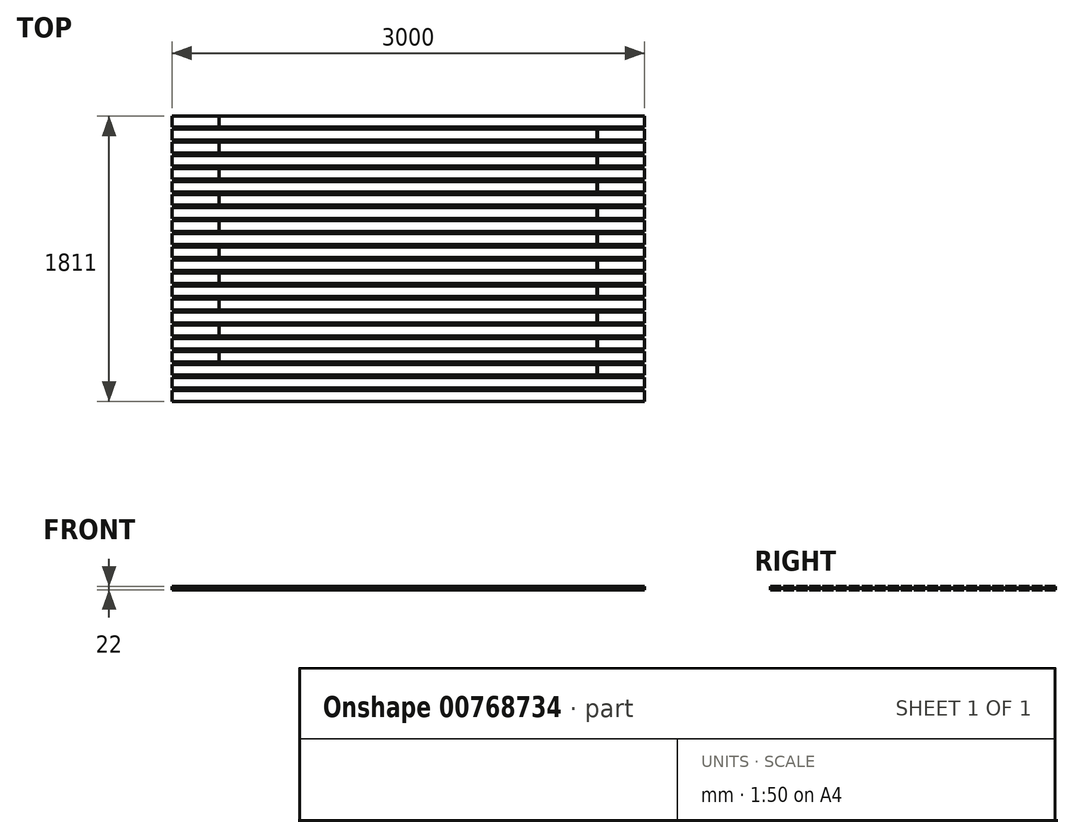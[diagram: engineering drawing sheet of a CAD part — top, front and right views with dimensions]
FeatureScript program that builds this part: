
annotation { "Feature Type Name" : "Feature", "Feature Type Description" : "" }
export const myFeature = defineFeature(function(context is Context, id is Id, definition is map)
    precondition{}
    {
        {
            var Q0;
            Q0=qCreatedBy(makeId("Top.planeOp"),FACE);
            var sketch = newSketch(context, id + "F0", { "sketchPlane" : qUnion([Q0])});
            skLineSegment(sketch, "E0.bottom", {"start": v(0, 0) * mm, "end": v(2700, 0) * mm});
            skLineSegment(sketch, "E0.top", {"start": v(0, 68) * mm, "end": v(2700, 68) * mm});
            skLineSegment(sketch, "E0.left", {"start": v(0, 0) * mm, "end": v(0, 68) * mm});
            skLineSegment(sketch, "E0.right", {"start": v(2700, 0) * mm, "end": v(2700, 68) * mm});
            skLineSegment(sketch, "E1.bottom", {"start": v(0, 83) * mm, "end": v(300, 83) * mm});
            skLineSegment(sketch, "E1.top", {"start": v(0, 151) * mm, "end": v(300, 151) * mm});
            skLineSegment(sketch, "E1.left", {"start": v(0, 83) * mm, "end": v(0, 151) * mm});
            skLineSegment(sketch, "E1.right", {"start": v(300, 83) * mm, "end": v(300, 151) * mm});
            skLineSegment(sketch, "E2.bottom", {"start": v(300, 151) * mm, "end": v(3000, 151) * mm});
            skLineSegment(sketch, "E2.top", {"start": v(300, 83) * mm, "end": v(3000, 83) * mm});
            skLineSegment(sketch, "E2.left", {"start": v(300, 151) * mm, "end": v(300, 83) * mm});
            skLineSegment(sketch, "E2.right", {"start": v(3000, 151) * mm, "end": v(3000, 83) * mm});
            skLineSegment(sketch, "E3.bottom", {"start": v(2700, 68) * mm, "end": v(3000, 68) * mm});
            skLineSegment(sketch, "E3.top", {"start": v(2700, 0) * mm, "end": v(3000, 0) * mm});
            skLineSegment(sketch, "E3.left", {"start": v(2700, 68) * mm, "end": v(2700, 0) * mm});
            skLineSegment(sketch, "E3.right", {"start": v(3000, 68) * mm, "end": v(3000, 0) * mm});
            skLineSegment(sketch, "E4.0.1.0", {"start": v(0, 249) * mm, "end": v(300, 249) * mm});
            skLineSegment(sketch, "E4.0.1.1", {"start": v(0, 234) * mm, "end": v(2700, 234) * mm});
            skLineSegment(sketch, "E4.0.1.2", {"start": v(300, 317) * mm, "end": v(3000, 317) * mm});
            skLineSegment(sketch, "E4.0.1.3", {"start": v(0, 317) * mm, "end": v(300, 317) * mm});
            skLineSegment(sketch, "E4.0.1.4", {"start": v(2700, 166) * mm, "end": v(3000, 166) * mm});
            skLineSegment(sketch, "E4.0.1.5", {"start": v(2700, 234) * mm, "end": v(3000, 234) * mm});
            skLineSegment(sketch, "E4.0.1.6", {"start": v(300, 249) * mm, "end": v(3000, 249) * mm});
            skLineSegment(sketch, "E4.0.1.7", {"start": v(0, 166) * mm, "end": v(2700, 166) * mm});
            skLineSegment(sketch, "E4.0.1.8", {"start": v(3000, 234) * mm, "end": v(3000, 166) * mm});
            skLineSegment(sketch, "E4.0.1.9", {"start": v(0, 166) * mm, "end": v(0, 234) * mm});
            skLineSegment(sketch, "E4.0.1.10", {"start": v(0, 249) * mm, "end": v(0, 317) * mm});
            skLineSegment(sketch, "E4.0.1.11", {"start": v(3000, 317) * mm, "end": v(3000, 249) * mm});
            skLineSegment(sketch, "E4.0.1.12", {"start": v(2700, 234) * mm, "end": v(2700, 166) * mm});
            skLineSegment(sketch, "E4.0.1.13", {"start": v(300, 317) * mm, "end": v(300, 249) * mm});
            skLineSegment(sketch, "E4.0.1.14", {"start": v(300, 249) * mm, "end": v(300, 317) * mm});
            skLineSegment(sketch, "E4.0.1.15", {"start": v(2700, 166) * mm, "end": v(2700, 234) * mm});
            skLineSegment(sketch, "E4.0.2.0", {"start": v(0, 415) * mm, "end": v(300, 415) * mm});
            skLineSegment(sketch, "E4.0.2.1", {"start": v(0, 400) * mm, "end": v(2700, 400) * mm});
            skLineSegment(sketch, "E4.0.2.2", {"start": v(300, 483) * mm, "end": v(3000, 483) * mm});
            skLineSegment(sketch, "E4.0.2.3", {"start": v(0, 483) * mm, "end": v(300, 483) * mm});
            skLineSegment(sketch, "E4.0.2.4", {"start": v(2700, 332) * mm, "end": v(3000, 332) * mm});
            skLineSegment(sketch, "E4.0.2.5", {"start": v(2700, 400) * mm, "end": v(3000, 400) * mm});
            skLineSegment(sketch, "E4.0.2.6", {"start": v(300, 415) * mm, "end": v(3000, 415) * mm});
            skLineSegment(sketch, "E4.0.2.7", {"start": v(0, 332) * mm, "end": v(2700, 332) * mm});
            skLineSegment(sketch, "E4.0.2.8", {"start": v(3000, 400) * mm, "end": v(3000, 332) * mm});
            skLineSegment(sketch, "E4.0.2.9", {"start": v(0, 332) * mm, "end": v(0, 400) * mm});
            skLineSegment(sketch, "E4.0.2.10", {"start": v(0, 415) * mm, "end": v(0, 483) * mm});
            skLineSegment(sketch, "E4.0.2.11", {"start": v(3000, 483) * mm, "end": v(3000, 415) * mm});
            skLineSegment(sketch, "E4.0.2.12", {"start": v(2700, 400) * mm, "end": v(2700, 332) * mm});
            skLineSegment(sketch, "E4.0.2.13", {"start": v(300, 483) * mm, "end": v(300, 415) * mm});
            skLineSegment(sketch, "E4.0.2.14", {"start": v(300, 415) * mm, "end": v(300, 483) * mm});
            skLineSegment(sketch, "E4.0.2.15", {"start": v(2700, 332) * mm, "end": v(2700, 400) * mm});
            skLineSegment(sketch, "E4.0.3.0", {"start": v(0, 581) * mm, "end": v(300, 581) * mm});
            skLineSegment(sketch, "E4.0.3.1", {"start": v(0, 566) * mm, "end": v(2700, 566) * mm});
            skLineSegment(sketch, "E4.0.3.2", {"start": v(300, 649) * mm, "end": v(3000, 649) * mm});
            skLineSegment(sketch, "E4.0.3.3", {"start": v(0, 649) * mm, "end": v(300, 649) * mm});
            skLineSegment(sketch, "E4.0.3.4", {"start": v(2700, 498) * mm, "end": v(3000, 498) * mm});
            skLineSegment(sketch, "E4.0.3.5", {"start": v(2700, 566) * mm, "end": v(3000, 566) * mm});
            skLineSegment(sketch, "E4.0.3.6", {"start": v(300, 581) * mm, "end": v(3000, 581) * mm});
            skLineSegment(sketch, "E4.0.3.7", {"start": v(0, 498) * mm, "end": v(2700, 498) * mm});
            skLineSegment(sketch, "E4.0.3.8", {"start": v(3000, 566) * mm, "end": v(3000, 498) * mm});
            skLineSegment(sketch, "E4.0.3.9", {"start": v(0, 498) * mm, "end": v(0, 566) * mm});
            skLineSegment(sketch, "E4.0.3.10", {"start": v(0, 581) * mm, "end": v(0, 649) * mm});
            skLineSegment(sketch, "E4.0.3.11", {"start": v(3000, 649) * mm, "end": v(3000, 581) * mm});
            skLineSegment(sketch, "E4.0.3.12", {"start": v(2700, 566) * mm, "end": v(2700, 498) * mm});
            skLineSegment(sketch, "E4.0.3.13", {"start": v(300, 649) * mm, "end": v(300, 581) * mm});
            skLineSegment(sketch, "E4.0.3.14", {"start": v(300, 581) * mm, "end": v(300, 649) * mm});
            skLineSegment(sketch, "E4.0.3.15", {"start": v(2700, 498) * mm, "end": v(2700, 566) * mm});
            skLineSegment(sketch, "E4.0.4.0", {"start": v(0, 747) * mm, "end": v(300, 747) * mm});
            skLineSegment(sketch, "E4.0.4.1", {"start": v(0, 732) * mm, "end": v(2700, 732) * mm});
            skLineSegment(sketch, "E4.0.4.2", {"start": v(300, 815) * mm, "end": v(3000, 815) * mm});
            skLineSegment(sketch, "E4.0.4.3", {"start": v(0, 815) * mm, "end": v(300, 815) * mm});
            skLineSegment(sketch, "E4.0.4.4", {"start": v(2700, 664) * mm, "end": v(3000, 664) * mm});
            skLineSegment(sketch, "E4.0.4.5", {"start": v(2700, 732) * mm, "end": v(3000, 732) * mm});
            skLineSegment(sketch, "E4.0.4.6", {"start": v(300, 747) * mm, "end": v(3000, 747) * mm});
            skLineSegment(sketch, "E4.0.4.7", {"start": v(0, 664) * mm, "end": v(2700, 664) * mm});
            skLineSegment(sketch, "E4.0.4.8", {"start": v(3000, 732) * mm, "end": v(3000, 664) * mm});
            skLineSegment(sketch, "E4.0.4.9", {"start": v(0, 664) * mm, "end": v(0, 732) * mm});
            skLineSegment(sketch, "E4.0.4.10", {"start": v(0, 747) * mm, "end": v(0, 815) * mm});
            skLineSegment(sketch, "E4.0.4.11", {"start": v(3000, 815) * mm, "end": v(3000, 747) * mm});
            skLineSegment(sketch, "E4.0.4.12", {"start": v(2700, 732) * mm, "end": v(2700, 664) * mm});
            skLineSegment(sketch, "E4.0.4.13", {"start": v(300, 815) * mm, "end": v(300, 747) * mm});
            skLineSegment(sketch, "E4.0.4.14", {"start": v(300, 747) * mm, "end": v(300, 815) * mm});
            skLineSegment(sketch, "E4.0.4.15", {"start": v(2700, 664) * mm, "end": v(2700, 732) * mm});
            skLineSegment(sketch, "E4.0.5.0", {"start": v(0, 913) * mm, "end": v(300, 913) * mm});
            skLineSegment(sketch, "E4.0.5.1", {"start": v(0, 898) * mm, "end": v(2700, 898) * mm});
            skLineSegment(sketch, "E4.0.5.2", {"start": v(300, 981) * mm, "end": v(3000, 981) * mm});
            skLineSegment(sketch, "E4.0.5.3", {"start": v(0, 981) * mm, "end": v(300, 981) * mm});
            skLineSegment(sketch, "E4.0.5.4", {"start": v(2700, 830) * mm, "end": v(3000, 830) * mm});
            skLineSegment(sketch, "E4.0.5.5", {"start": v(2700, 898) * mm, "end": v(3000, 898) * mm});
            skLineSegment(sketch, "E4.0.5.6", {"start": v(300, 913) * mm, "end": v(3000, 913) * mm});
            skLineSegment(sketch, "E4.0.5.7", {"start": v(0, 830) * mm, "end": v(2700, 830) * mm});
            skLineSegment(sketch, "E4.0.5.8", {"start": v(3000, 898) * mm, "end": v(3000, 830) * mm});
            skLineSegment(sketch, "E4.0.5.9", {"start": v(0, 830) * mm, "end": v(0, 898) * mm});
            skLineSegment(sketch, "E4.0.5.10", {"start": v(0, 913) * mm, "end": v(0, 981) * mm});
            skLineSegment(sketch, "E4.0.5.11", {"start": v(3000, 981) * mm, "end": v(3000, 913) * mm});
            skLineSegment(sketch, "E4.0.5.12", {"start": v(2700, 898) * mm, "end": v(2700, 830) * mm});
            skLineSegment(sketch, "E4.0.5.13", {"start": v(300, 981) * mm, "end": v(300, 913) * mm});
            skLineSegment(sketch, "E4.0.5.14", {"start": v(300, 913) * mm, "end": v(300, 981) * mm});
            skLineSegment(sketch, "E4.0.5.15", {"start": v(2700, 830) * mm, "end": v(2700, 898) * mm});
            skLineSegment(sketch, "E4.0.6.0", {"start": v(0, 1079) * mm, "end": v(300, 1079) * mm});
            skLineSegment(sketch, "E4.0.6.1", {"start": v(0, 1064) * mm, "end": v(2700, 1064) * mm});
            skLineSegment(sketch, "E4.0.6.2", {"start": v(300, 1147) * mm, "end": v(3000, 1147) * mm});
            skLineSegment(sketch, "E4.0.6.3", {"start": v(0, 1147) * mm, "end": v(300, 1147) * mm});
            skLineSegment(sketch, "E4.0.6.4", {"start": v(2700, 996) * mm, "end": v(3000, 996) * mm});
            skLineSegment(sketch, "E4.0.6.5", {"start": v(2700, 1064) * mm, "end": v(3000, 1064) * mm});
            skLineSegment(sketch, "E4.0.6.6", {"start": v(300, 1079) * mm, "end": v(3000, 1079) * mm});
            skLineSegment(sketch, "E4.0.6.7", {"start": v(0, 996) * mm, "end": v(2700, 996) * mm});
            skLineSegment(sketch, "E4.0.6.8", {"start": v(3000, 1064) * mm, "end": v(3000, 996) * mm});
            skLineSegment(sketch, "E4.0.6.9", {"start": v(0, 996) * mm, "end": v(0, 1064) * mm});
            skLineSegment(sketch, "E4.0.6.10", {"start": v(0, 1079) * mm, "end": v(0, 1147) * mm});
            skLineSegment(sketch, "E4.0.6.11", {"start": v(3000, 1147) * mm, "end": v(3000, 1079) * mm});
            skLineSegment(sketch, "E4.0.6.12", {"start": v(2700, 1064) * mm, "end": v(2700, 996) * mm});
            skLineSegment(sketch, "E4.0.6.13", {"start": v(300, 1147) * mm, "end": v(300, 1079) * mm});
            skLineSegment(sketch, "E4.0.6.14", {"start": v(300, 1079) * mm, "end": v(300, 1147) * mm});
            skLineSegment(sketch, "E4.0.6.15", {"start": v(2700, 996) * mm, "end": v(2700, 1064) * mm});
            skLineSegment(sketch, "E4.0.7.0", {"start": v(0, 1245) * mm, "end": v(300, 1245) * mm});
            skLineSegment(sketch, "E4.0.7.1", {"start": v(0, 1230) * mm, "end": v(2700, 1230) * mm});
            skLineSegment(sketch, "E4.0.7.2", {"start": v(300, 1313) * mm, "end": v(3000, 1313) * mm});
            skLineSegment(sketch, "E4.0.7.3", {"start": v(0, 1313) * mm, "end": v(300, 1313) * mm});
            skLineSegment(sketch, "E4.0.7.4", {"start": v(2700, 1162) * mm, "end": v(3000, 1162) * mm});
            skLineSegment(sketch, "E4.0.7.5", {"start": v(2700, 1230) * mm, "end": v(3000, 1230) * mm});
            skLineSegment(sketch, "E4.0.7.6", {"start": v(300, 1245) * mm, "end": v(3000, 1245) * mm});
            skLineSegment(sketch, "E4.0.7.7", {"start": v(0, 1162) * mm, "end": v(2700, 1162) * mm});
            skLineSegment(sketch, "E4.0.7.8", {"start": v(3000, 1230) * mm, "end": v(3000, 1162) * mm});
            skLineSegment(sketch, "E4.0.7.9", {"start": v(0, 1162) * mm, "end": v(0, 1230) * mm});
            skLineSegment(sketch, "E4.0.7.10", {"start": v(0, 1245) * mm, "end": v(0, 1313) * mm});
            skLineSegment(sketch, "E4.0.7.11", {"start": v(3000, 1313) * mm, "end": v(3000, 1245) * mm});
            skLineSegment(sketch, "E4.0.7.12", {"start": v(2700, 1230) * mm, "end": v(2700, 1162) * mm});
            skLineSegment(sketch, "E4.0.7.13", {"start": v(300, 1313) * mm, "end": v(300, 1245) * mm});
            skLineSegment(sketch, "E4.0.7.14", {"start": v(300, 1245) * mm, "end": v(300, 1313) * mm});
            skLineSegment(sketch, "E4.0.7.15", {"start": v(2700, 1162) * mm, "end": v(2700, 1230) * mm});
            skLineSegment(sketch, "E4.0.8.0", {"start": v(0, 1411) * mm, "end": v(300, 1411) * mm});
            skLineSegment(sketch, "E4.0.8.1", {"start": v(0, 1396) * mm, "end": v(2700, 1396) * mm});
            skLineSegment(sketch, "E4.0.8.2", {"start": v(300, 1479) * mm, "end": v(3000, 1479) * mm});
            skLineSegment(sketch, "E4.0.8.3", {"start": v(0, 1479) * mm, "end": v(300, 1479) * mm});
            skLineSegment(sketch, "E4.0.8.4", {"start": v(2700, 1328) * mm, "end": v(3000, 1328) * mm});
            skLineSegment(sketch, "E4.0.8.5", {"start": v(2700, 1396) * mm, "end": v(3000, 1396) * mm});
            skLineSegment(sketch, "E4.0.8.6", {"start": v(300, 1411) * mm, "end": v(3000, 1411) * mm});
            skLineSegment(sketch, "E4.0.8.7", {"start": v(0, 1328) * mm, "end": v(2700, 1328) * mm});
            skLineSegment(sketch, "E4.0.8.8", {"start": v(3000, 1396) * mm, "end": v(3000, 1328) * mm});
            skLineSegment(sketch, "E4.0.8.9", {"start": v(0, 1328) * mm, "end": v(0, 1396) * mm});
            skLineSegment(sketch, "E4.0.8.10", {"start": v(0, 1411) * mm, "end": v(0, 1479) * mm});
            skLineSegment(sketch, "E4.0.8.11", {"start": v(3000, 1479) * mm, "end": v(3000, 1411) * mm});
            skLineSegment(sketch, "E4.0.8.12", {"start": v(2700, 1396) * mm, "end": v(2700, 1328) * mm});
            skLineSegment(sketch, "E4.0.8.13", {"start": v(300, 1479) * mm, "end": v(300, 1411) * mm});
            skLineSegment(sketch, "E4.0.8.14", {"start": v(300, 1411) * mm, "end": v(300, 1479) * mm});
            skLineSegment(sketch, "E4.0.8.15", {"start": v(2700, 1328) * mm, "end": v(2700, 1396) * mm});
            skLineSegment(sketch, "E4.0.9.0", {"start": v(0, 1577) * mm, "end": v(300, 1577) * mm});
            skLineSegment(sketch, "E4.0.9.1", {"start": v(0, 1562) * mm, "end": v(2700, 1562) * mm});
            skLineSegment(sketch, "E4.0.9.2", {"start": v(300, 1645) * mm, "end": v(3000, 1645) * mm});
            skLineSegment(sketch, "E4.0.9.3", {"start": v(0, 1645) * mm, "end": v(300, 1645) * mm});
            skLineSegment(sketch, "E4.0.9.4", {"start": v(2700, 1494) * mm, "end": v(3000, 1494) * mm});
            skLineSegment(sketch, "E4.0.9.5", {"start": v(2700, 1562) * mm, "end": v(3000, 1562) * mm});
            skLineSegment(sketch, "E4.0.9.6", {"start": v(300, 1577) * mm, "end": v(3000, 1577) * mm});
            skLineSegment(sketch, "E4.0.9.7", {"start": v(0, 1494) * mm, "end": v(2700, 1494) * mm});
            skLineSegment(sketch, "E4.0.9.8", {"start": v(3000, 1562) * mm, "end": v(3000, 1494) * mm});
            skLineSegment(sketch, "E4.0.9.9", {"start": v(0, 1494) * mm, "end": v(0, 1562) * mm});
            skLineSegment(sketch, "E4.0.9.10", {"start": v(0, 1577) * mm, "end": v(0, 1645) * mm});
            skLineSegment(sketch, "E4.0.9.11", {"start": v(3000, 1645) * mm, "end": v(3000, 1577) * mm});
            skLineSegment(sketch, "E4.0.9.12", {"start": v(2700, 1562) * mm, "end": v(2700, 1494) * mm});
            skLineSegment(sketch, "E4.0.9.13", {"start": v(300, 1645) * mm, "end": v(300, 1577) * mm});
            skLineSegment(sketch, "E4.0.9.14", {"start": v(300, 1577) * mm, "end": v(300, 1645) * mm});
            skLineSegment(sketch, "E4.0.9.15", {"start": v(2700, 1494) * mm, "end": v(2700, 1562) * mm});
            skLineSegment(sketch, "E4.direction1", {"start": v(0, 0) * mm, "end": v(25, 0) * mm, "construction": true});
            skLineSegment(sketch, "E4.direction2", {"start": v(0, 0) * mm, "end": v(0, 166) * mm, "construction": true});
            skLineSegment(sketch, "E5.0.0.10", {"start": v(0, 1743) * mm, "end": v(300, 1743) * mm});
            skLineSegment(sketch, "E5.3.0.10", {"start": v(0, 1728) * mm, "end": v(2700, 1728) * mm});
            skLineSegment(sketch, "E5.6.0.10", {"start": v(300, 1811) * mm, "end": v(3000, 1811) * mm});
            skLineSegment(sketch, "E5.9.0.10", {"start": v(0, 1811) * mm, "end": v(300, 1811) * mm});
            skLineSegment(sketch, "E5.12.0.10", {"start": v(2700, 1660) * mm, "end": v(3000, 1660) * mm});
            skLineSegment(sketch, "E5.15.0.10", {"start": v(2700, 1728) * mm, "end": v(3000, 1728) * mm});
            skLineSegment(sketch, "E5.18.0.10", {"start": v(300, 1743) * mm, "end": v(3000, 1743) * mm});
            skLineSegment(sketch, "E5.21.0.10", {"start": v(0, 1660) * mm, "end": v(2700, 1660) * mm});
            skLineSegment(sketch, "E5.24.0.10", {"start": v(3000, 1728) * mm, "end": v(3000, 1660) * mm});
            skLineSegment(sketch, "E5.27.0.10", {"start": v(0, 1660) * mm, "end": v(0, 1728) * mm});
            skLineSegment(sketch, "E5.30.0.10", {"start": v(0, 1743) * mm, "end": v(0, 1811) * mm});
            skLineSegment(sketch, "E5.33.0.10", {"start": v(3000, 1811) * mm, "end": v(3000, 1743) * mm});
            skLineSegment(sketch, "E5.36.0.10", {"start": v(2700, 1728) * mm, "end": v(2700, 1660) * mm});
            skLineSegment(sketch, "E5.39.0.10", {"start": v(300, 1811) * mm, "end": v(300, 1743) * mm});
            skLineSegment(sketch, "E5.42.0.10", {"start": v(300, 1743) * mm, "end": v(300, 1811) * mm});
            skLineSegment(sketch, "E5.45.0.10", {"start": v(2700, 1660) * mm, "end": v(2700, 1728) * mm});
            skLineSegment(sketch, "E6.bottom", {"start": v(300, 151) * mm, "end": v(297.5, 151) * mm});
            skLineSegment(sketch, "E6.top", {"start": v(300, 83) * mm, "end": v(297.5, 83) * mm});
            skLineSegment(sketch, "E6.right", {"start": v(297.5, 151) * mm, "end": v(297.5, 83) * mm});
            skLineSegment(sketch, "E7.bottom", {"start": v(2700, 68) * mm, "end": v(2702.5, 68) * mm});
            skLineSegment(sketch, "E7.top", {"start": v(2700, 0) * mm, "end": v(2702.5, 0) * mm});
            skLineSegment(sketch, "E7.right", {"start": v(2702.5, 68) * mm, "end": v(2702.5, 0) * mm});
            skLineSegment(sketch, "E8.0.1.0", {"start": v(2702.5, 234) * mm, "end": v(2702.5, 166) * mm});
            skLineSegment(sketch, "E8.0.1.2", {"start": v(2700, 166) * mm, "end": v(2702.5, 166) * mm});
            skLineSegment(sketch, "E8.0.1.3", {"start": v(2700, 234) * mm, "end": v(2702.5, 234) * mm});
            skLineSegment(sketch, "E8.0.1.4", {"start": v(297.5, 317) * mm, "end": v(297.5, 249) * mm});
            skLineSegment(sketch, "E8.0.1.6", {"start": v(300, 317) * mm, "end": v(297.5, 317) * mm});
            skLineSegment(sketch, "E8.0.1.7", {"start": v(300, 249) * mm, "end": v(297.5, 249) * mm});
            skLineSegment(sketch, "E8.0.2.0", {"start": v(2702.5, 400) * mm, "end": v(2702.5, 332) * mm});
            skLineSegment(sketch, "E8.0.2.2", {"start": v(2700, 332) * mm, "end": v(2702.5, 332) * mm});
            skLineSegment(sketch, "E8.0.2.3", {"start": v(2700, 400) * mm, "end": v(2702.5, 400) * mm});
            skLineSegment(sketch, "E8.0.2.4", {"start": v(297.5, 483) * mm, "end": v(297.5, 415) * mm});
            skLineSegment(sketch, "E8.0.2.6", {"start": v(300, 483) * mm, "end": v(297.5, 483) * mm});
            skLineSegment(sketch, "E8.0.2.7", {"start": v(300, 415) * mm, "end": v(297.5, 415) * mm});
            skLineSegment(sketch, "E8.0.3.0", {"start": v(2702.5, 566) * mm, "end": v(2702.5, 498) * mm});
            skLineSegment(sketch, "E8.0.3.2", {"start": v(2700, 498) * mm, "end": v(2702.5, 498) * mm});
            skLineSegment(sketch, "E8.0.3.3", {"start": v(2700, 566) * mm, "end": v(2702.5, 566) * mm});
            skLineSegment(sketch, "E8.0.3.4", {"start": v(297.5, 649) * mm, "end": v(297.5, 581) * mm});
            skLineSegment(sketch, "E8.0.3.6", {"start": v(300, 649) * mm, "end": v(297.5, 649) * mm});
            skLineSegment(sketch, "E8.0.3.7", {"start": v(300, 581) * mm, "end": v(297.5, 581) * mm});
            skLineSegment(sketch, "E8.0.4.0", {"start": v(2702.5, 732) * mm, "end": v(2702.5, 664) * mm});
            skLineSegment(sketch, "E8.0.4.2", {"start": v(2700, 664) * mm, "end": v(2702.5, 664) * mm});
            skLineSegment(sketch, "E8.0.4.3", {"start": v(2700, 732) * mm, "end": v(2702.5, 732) * mm});
            skLineSegment(sketch, "E8.0.4.4", {"start": v(297.5, 815) * mm, "end": v(297.5, 747) * mm});
            skLineSegment(sketch, "E8.0.4.6", {"start": v(300, 815) * mm, "end": v(297.5, 815) * mm});
            skLineSegment(sketch, "E8.0.4.7", {"start": v(300, 747) * mm, "end": v(297.5, 747) * mm});
            skLineSegment(sketch, "E8.0.5.0", {"start": v(2702.5, 898) * mm, "end": v(2702.5, 830) * mm});
            skLineSegment(sketch, "E8.0.5.2", {"start": v(2700, 830) * mm, "end": v(2702.5, 830) * mm});
            skLineSegment(sketch, "E8.0.5.3", {"start": v(2700, 898) * mm, "end": v(2702.5, 898) * mm});
            skLineSegment(sketch, "E8.0.5.4", {"start": v(297.5, 981) * mm, "end": v(297.5, 913) * mm});
            skLineSegment(sketch, "E8.0.5.6", {"start": v(300, 981) * mm, "end": v(297.5, 981) * mm});
            skLineSegment(sketch, "E8.0.5.7", {"start": v(300, 913) * mm, "end": v(297.5, 913) * mm});
            skLineSegment(sketch, "E8.0.6.0", {"start": v(2702.5, 1064) * mm, "end": v(2702.5, 996) * mm});
            skLineSegment(sketch, "E8.0.6.2", {"start": v(2700, 996) * mm, "end": v(2702.5, 996) * mm});
            skLineSegment(sketch, "E8.0.6.3", {"start": v(2700, 1064) * mm, "end": v(2702.5, 1064) * mm});
            skLineSegment(sketch, "E8.0.6.4", {"start": v(297.5, 1147) * mm, "end": v(297.5, 1079) * mm});
            skLineSegment(sketch, "E8.0.6.6", {"start": v(300, 1147) * mm, "end": v(297.5, 1147) * mm});
            skLineSegment(sketch, "E8.0.6.7", {"start": v(300, 1079) * mm, "end": v(297.5, 1079) * mm});
            skLineSegment(sketch, "E8.0.7.0", {"start": v(2702.5, 1230) * mm, "end": v(2702.5, 1162) * mm});
            skLineSegment(sketch, "E8.0.7.2", {"start": v(2700, 1162) * mm, "end": v(2702.5, 1162) * mm});
            skLineSegment(sketch, "E8.0.7.3", {"start": v(2700, 1230) * mm, "end": v(2702.5, 1230) * mm});
            skLineSegment(sketch, "E8.0.7.4", {"start": v(297.5, 1313) * mm, "end": v(297.5, 1245) * mm});
            skLineSegment(sketch, "E8.0.7.6", {"start": v(300, 1313) * mm, "end": v(297.5, 1313) * mm});
            skLineSegment(sketch, "E8.0.7.7", {"start": v(300, 1245) * mm, "end": v(297.5, 1245) * mm});
            skLineSegment(sketch, "E8.0.8.0", {"start": v(2702.5, 1396) * mm, "end": v(2702.5, 1328) * mm});
            skLineSegment(sketch, "E8.0.8.2", {"start": v(2700, 1328) * mm, "end": v(2702.5, 1328) * mm});
            skLineSegment(sketch, "E8.0.8.3", {"start": v(2700, 1396) * mm, "end": v(2702.5, 1396) * mm});
            skLineSegment(sketch, "E8.0.8.4", {"start": v(297.5, 1479) * mm, "end": v(297.5, 1411) * mm});
            skLineSegment(sketch, "E8.0.8.6", {"start": v(300, 1479) * mm, "end": v(297.5, 1479) * mm});
            skLineSegment(sketch, "E8.0.8.7", {"start": v(300, 1411) * mm, "end": v(297.5, 1411) * mm});
            skLineSegment(sketch, "E8.0.9.0", {"start": v(2702.5, 1562) * mm, "end": v(2702.5, 1494) * mm});
            skLineSegment(sketch, "E8.0.9.2", {"start": v(2700, 1494) * mm, "end": v(2702.5, 1494) * mm});
            skLineSegment(sketch, "E8.0.9.3", {"start": v(2700, 1562) * mm, "end": v(2702.5, 1562) * mm});
            skLineSegment(sketch, "E8.0.9.4", {"start": v(297.5, 1645) * mm, "end": v(297.5, 1577) * mm});
            skLineSegment(sketch, "E8.0.9.6", {"start": v(300, 1645) * mm, "end": v(297.5, 1645) * mm});
            skLineSegment(sketch, "E8.0.9.7", {"start": v(300, 1577) * mm, "end": v(297.5, 1577) * mm});
            skLineSegment(sketch, "E8.0.10.0", {"start": v(2702.5, 1728) * mm, "end": v(2702.5, 1660) * mm});
            skLineSegment(sketch, "E8.0.10.2", {"start": v(2700, 1660) * mm, "end": v(2702.5, 1660) * mm});
            skLineSegment(sketch, "E8.0.10.3", {"start": v(2700, 1728) * mm, "end": v(2702.5, 1728) * mm});
            skLineSegment(sketch, "E8.0.10.4", {"start": v(297.5, 1811) * mm, "end": v(297.5, 1743) * mm});
            skLineSegment(sketch, "E8.0.10.6", {"start": v(300, 1811) * mm, "end": v(297.5, 1811) * mm});
            skLineSegment(sketch, "E8.0.10.7", {"start": v(300, 1743) * mm, "end": v(297.5, 1743) * mm});
            skLineSegment(sketch, "E8.direction1", {"start": v(2702.5, 0) * mm, "end": v(2909.5, 0) * mm, "construction": true});
            skSolve(sketch);
        }
        {
            var Q0;
            Q0 = qSketchRegion(id + "F0", true);
            extrude(context, id + "F1", {"entities" : qUnion([Q0]), "depth" : 22 * mm, "offsetDistance" : 25 * mm});
        }
        {
            var Q0;
            Q0=makeQuery(id+"F0.imprint","IMPRINT",FACE,{"disambiguationData":[TD([[makeQuery(id+"F0.imprint","IMPRINT",EDGE,{"derivedFrom":sQuery(id+"F0.wireOp",EDGE,"E6.bottom")}),1.0]])]});
            var Q1;
            Q1=makeQuery(id+"F0.imprint","IMPRINT",FACE,{"disambiguationData":[TD([[makeQuery(id+"F0.imprint","IMPRINT",EDGE,{"derivedFrom":sQuery(id+"F0.wireOp",EDGE,"E8.0.1.4")}),1.0]])]});
            var Q2;
            Q2=makeQuery(id+"F0.imprint","IMPRINT",FACE,{"disambiguationData":[TD([[makeQuery(id+"F0.imprint","IMPRINT",EDGE,{"derivedFrom":sQuery(id+"F0.wireOp",EDGE,"E8.0.2.4")}),1.0]])]});
            var Q3;
            Q3=makeQuery(id+"F0.imprint","IMPRINT",FACE,{"disambiguationData":[TD([[makeQuery(id+"F0.imprint","IMPRINT",EDGE,{"derivedFrom":sQuery(id+"F0.wireOp",EDGE,"E8.0.3.4")}),1.0]])]});
            var Q4;
            Q4=makeQuery(id+"F0.imprint","IMPRINT",FACE,{"disambiguationData":[TD([[makeQuery(id+"F0.imprint","IMPRINT",EDGE,{"derivedFrom":sQuery(id+"F0.wireOp",EDGE,"E8.0.4.4")}),1.0]])]});
            var Q5;
            Q5=makeQuery(id+"F0.imprint","IMPRINT",FACE,{"disambiguationData":[TD([[makeQuery(id+"F0.imprint","IMPRINT",EDGE,{"derivedFrom":sQuery(id+"F0.wireOp",EDGE,"E8.0.5.4")}),1.0]])]});
            var Q6;
            Q6=makeQuery(id+"F0.imprint","IMPRINT",FACE,{"disambiguationData":[TD([[makeQuery(id+"F0.imprint","IMPRINT",EDGE,{"derivedFrom":sQuery(id+"F0.wireOp",EDGE,"E8.0.6.4")}),1.0]])]});
            var Q7;
            Q7=makeQuery(id+"F0.imprint","IMPRINT",FACE,{"disambiguationData":[TD([[makeQuery(id+"F0.imprint","IMPRINT",EDGE,{"derivedFrom":sQuery(id+"F0.wireOp",EDGE,"E8.0.7.4")}),1.0]])]});
            var Q8;
            Q8=makeQuery(id+"F0.imprint","IMPRINT",FACE,{"disambiguationData":[TD([[makeQuery(id+"F0.imprint","IMPRINT",EDGE,{"derivedFrom":sQuery(id+"F0.wireOp",EDGE,"E8.0.8.4")}),1.0]])]});
            var Q9;
            Q9=makeQuery(id+"F0.imprint","IMPRINT",FACE,{"disambiguationData":[TD([[makeQuery(id+"F0.imprint","IMPRINT",EDGE,{"derivedFrom":sQuery(id+"F0.wireOp",EDGE,"E8.0.9.4")}),1.0]])]});
            var Q10;
            Q10=makeQuery(id+"F0.imprint","IMPRINT",FACE,{"disambiguationData":[TD([[makeQuery(id+"F0.imprint","IMPRINT",EDGE,{"derivedFrom":sQuery(id+"F0.wireOp",EDGE,"E8.0.10.4")}),1.0]])]});
            var Q11;
            Q11=makeQuery(id+"F0.imprint","IMPRINT",FACE,{"disambiguationData":[TD([[makeQuery(id+"F0.imprint","IMPRINT",EDGE,{"derivedFrom":sQuery(id+"F0.wireOp",EDGE,"E8.0.10.0")}),-1.0]])]});
            var Q12;
            Q12=makeQuery(id+"F0.imprint","IMPRINT",FACE,{"disambiguationData":[TD([[makeQuery(id+"F0.imprint","IMPRINT",EDGE,{"derivedFrom":sQuery(id+"F0.wireOp",EDGE,"E8.0.9.0")}),-1.0]])]});
            var Q13;
            Q13=makeQuery(id+"F0.imprint","IMPRINT",FACE,{"disambiguationData":[TD([[makeQuery(id+"F0.imprint","IMPRINT",EDGE,{"derivedFrom":sQuery(id+"F0.wireOp",EDGE,"E8.0.8.0")}),-1.0]])]});
            var Q14;
            Q14=makeQuery(id+"F0.imprint","IMPRINT",FACE,{"disambiguationData":[TD([[makeQuery(id+"F0.imprint","IMPRINT",EDGE,{"derivedFrom":sQuery(id+"F0.wireOp",EDGE,"E8.0.7.0")}),-1.0]])]});
            var Q15;
            Q15=makeQuery(id+"F0.imprint","IMPRINT",FACE,{"disambiguationData":[TD([[makeQuery(id+"F0.imprint","IMPRINT",EDGE,{"derivedFrom":sQuery(id+"F0.wireOp",EDGE,"E8.0.6.0")}),-1.0]])]});
            var Q16;
            Q16=makeQuery(id+"F0.imprint","IMPRINT",FACE,{"disambiguationData":[TD([[makeQuery(id+"F0.imprint","IMPRINT",EDGE,{"derivedFrom":sQuery(id+"F0.wireOp",EDGE,"E8.0.5.0")}),-1.0]])]});
            var Q17;
            Q17=makeQuery(id+"F0.imprint","IMPRINT",FACE,{"disambiguationData":[TD([[makeQuery(id+"F0.imprint","IMPRINT",EDGE,{"derivedFrom":sQuery(id+"F0.wireOp",EDGE,"E8.0.4.0")}),-1.0]])]});
            var Q18;
            Q18=makeQuery(id+"F0.imprint","IMPRINT",FACE,{"disambiguationData":[TD([[makeQuery(id+"F0.imprint","IMPRINT",EDGE,{"derivedFrom":sQuery(id+"F0.wireOp",EDGE,"E8.0.3.0")}),-1.0]])]});
            var Q19;
            Q19=makeQuery(id+"F0.imprint","IMPRINT",FACE,{"disambiguationData":[TD([[makeQuery(id+"F0.imprint","IMPRINT",EDGE,{"derivedFrom":sQuery(id+"F0.wireOp",EDGE,"E8.0.2.0")}),-1.0]])]});
            var Q20;
            Q20=makeQuery(id+"F0.imprint","IMPRINT",FACE,{"disambiguationData":[TD([[makeQuery(id+"F0.imprint","IMPRINT",EDGE,{"derivedFrom":sQuery(id+"F0.wireOp",EDGE,"E8.0.1.0")}),-1.0]])]});
            var Q21;
            Q21=makeQuery(id+"F0.imprint","IMPRINT",FACE,{"disambiguationData":[TD([[makeQuery(id+"F0.imprint","IMPRINT",EDGE,{"derivedFrom":sQuery(id+"F0.wireOp",EDGE,"E7.bottom")}),-1.0]])]});
            extrude(context, id + "F2", {"entities" : qUnion([Q0, Q1, Q2, Q3, Q4, Q5, Q6, Q7, Q8, Q9, Q10, Q11, Q12, Q13, Q14, Q15, Q16, Q17, Q18, Q19, Q20, Q21]), "operationType" : NewBodyOperationType.REMOVE, "depth" : 25 * mm, "offsetDistance" : 25 * mm});
        }
    });
